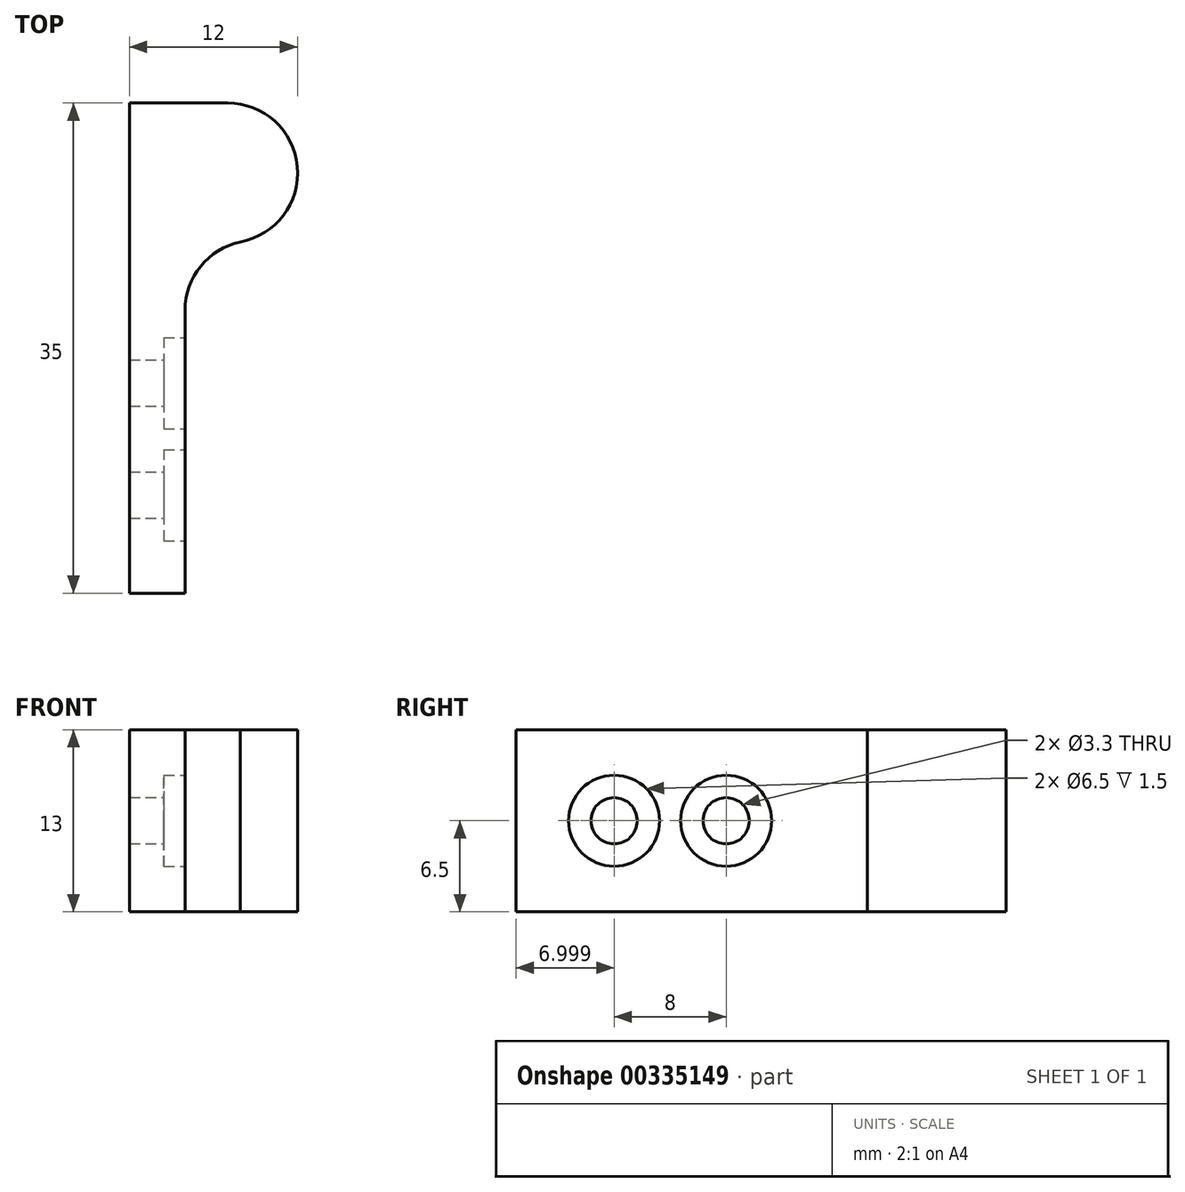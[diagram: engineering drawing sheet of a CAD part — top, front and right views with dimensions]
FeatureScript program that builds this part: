
annotation { "Feature Type Name" : "Feature", "Feature Type Description" : "" }
export const myFeature = defineFeature(function(context is Context, id is Id, definition is map)
    precondition{}
    {
        {
            var Q0;
            Q0=qCreatedBy(makeId("Top.planeOp"),FACE);
            var sketch = newSketch(context, id + "F0", { "sketchPlane" : qUnion([Q0])});
            skLineSegment(sketch, "E0", {"start": v(-0.82, 5.85) * mm, "end": v(6.18, 5.85) * mm});
            skArc(sketch, "E1", {"start": v(6.18, 5.85) * mm, "mid": v(11.16, 1.3) * mm, "end": v(7.1, -4.07) * mm});
            skLineSegment(sketch, "E2", {"start": v(-0.82, 5.85) * mm, "end": v(-0.82, -29.15) * mm});
            skLineSegment(sketch, "E3", {"start": v(-0.82, -29.15) * mm, "end": v(3.14, -29.15) * mm});
            skLineSegment(sketch, "E4", {"start": v(7.1, -4.07) * mm, "end": v(3.14, -4.07) * mm});
            skPoint(sketch, "E4.endSnap0", {"position": v(3.14, -29.15) * mm});
            skLineSegment(sketch, "E5", {"start": v(3.14, -4.07) * mm, "end": v(3.14, -29.15) * mm});
            skCircle(sketch, "E6", {"center": v(6.18, 0.85) * mm, "radius": 1.25 * mm, "construction": true});
            skSolve(sketch);
        }
        {
            var Q0;
            Q0 = qSketchRegion(id + "F0", true);
            extrude(context, id + "F1", {"entities" : qUnion([Q0]), "depth" : 13 * mm});
        }
        {
            var Q0;
            Q0=makeQuery(id+"F1.opExtrude","SWEPT_EDGE",EDGE,{"disambiguationData":[OSD([sQuery(id+"F0.wireOp",EDGE,"E4"),sQuery(id+"F0.wireOp",EDGE,"E5")])]});
            fillet(context, id + "F2", {"entities" : qUnion([Q0]), "radius" : 5 * mm, "tangentPropagation" : true, "allowEdgeOverflow" : false});
        }
        {
            var Q0;
            Q0=makeQuery(id+"F1.opExtrude","SWEPT_FACE",FACE,{"disambiguationData":[OSD([sQuery(id+"F0.wireOp",EDGE,"E5")])]});
            var sketch = newSketch(context, id + "F3", { "sketchPlane" : qUnion([Q0])});
            skPoint(sketch, "E7", {"position": v(-22.15, 6.5) * mm});
            skPoint(sketch, "E7.positionSnap0", {"position": v(-29.15, 6.5) * mm});
            skPoint(sketch, "E8", {"position": v(-14.15, 6.5) * mm});
            skSolve(sketch);
        }
        {
            var Q0;
            Q0=sQuery(id+"F3.wireOp",VERTEX,"E7");
            var Q1;
            Q1=sQuery(id+"F3.wireOp",VERTEX,"E8");
            var Q2;
            Q2=makeQuery(id+"F1.opExtrude","SWEPT_BODY",BODY,{"disambiguationData":[OSD([sQuery(id+"F0.wireOp",EDGE,"E0"),sQuery(id+"F0.wireOp",EDGE,"E1"),sQuery(id+"F0.wireOp",EDGE,"E2"),sQuery(id+"F0.wireOp",EDGE,"E3"),sQuery(id+"F0.wireOp",EDGE,"E4"),sQuery(id+"F0.wireOp",EDGE,"E5"),sQuery(id+"F0.wireOp",EDGE,"E6")])]});
            hole(context, id + "F4", {"style" : HoleStyle.C_BORE, "endStyle" : HoleEndStyle.THROUGH, "holeDiameter" : 3.3 * mm, "cBoreDiameter" : 6.5 * mm, "cBoreDepth" : 1.5 * mm, "isTappedThrough" : true, "tappedDepth" : 12 * mm, "tapClearance" : 3, "locations" : qUnion([Q0, Q1]), "scope" : qUnion([Q2])});
        }
    });
